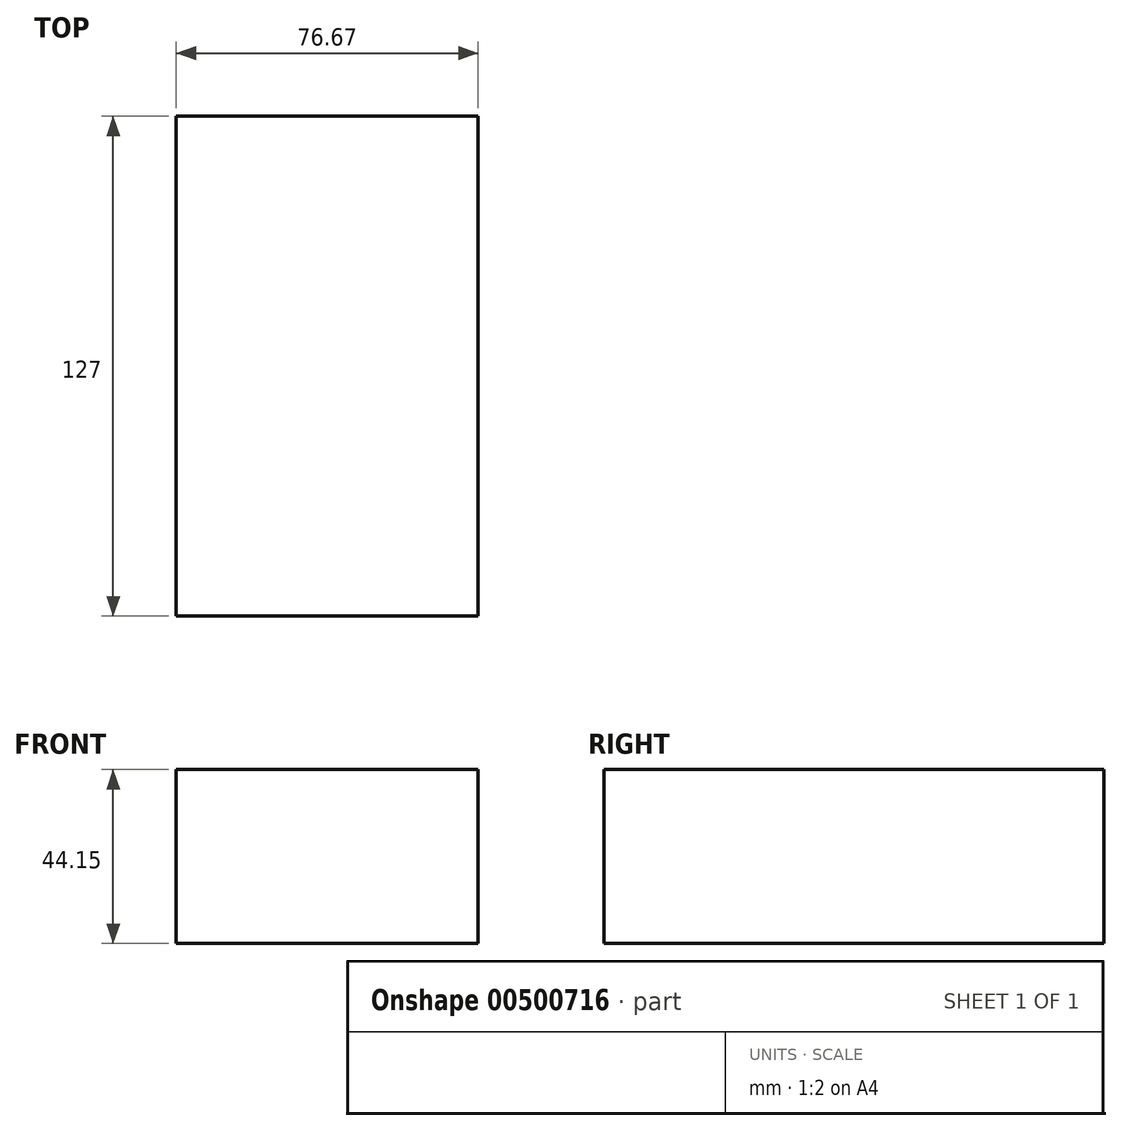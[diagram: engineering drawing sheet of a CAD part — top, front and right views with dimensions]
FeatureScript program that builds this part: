
annotation { "Feature Type Name" : "Feature", "Feature Type Description" : "" }
export const myFeature = defineFeature(function(context is Context, id is Id, definition is map)
    precondition{}
    {
        {
            var Q0;
            Q0=qCreatedBy(makeId("Front.planeOp"),FACE);
            var sketch = newSketch(context, id + "F0", { "sketchPlane" : qUnion([Q0])});
            skLineSegment(sketch, "E0.bottom", {"start": v(-36.6, 22.22) * mm, "end": v(40.08, 22.22) * mm});
            skLineSegment(sketch, "E0.top", {"start": v(-36.6, -21.93) * mm, "end": v(40.08, -21.93) * mm});
            skLineSegment(sketch, "E0.left", {"start": v(-36.6, 22.22) * mm, "end": v(-36.6, -21.93) * mm});
            skLineSegment(sketch, "E0.right", {"start": v(40.08, 22.22) * mm, "end": v(40.08, -21.93) * mm});
            skSolve(sketch);
        }
        {
            var Q0;
            Q0=makeQuery(id+"F0.imprint","IMPRINT",FACE,{"disambiguationData":[TD([[makeQuery(id+"F0.imprint","IMPRINT",EDGE,{"derivedFrom":sQuery(id+"F0.wireOp",EDGE,"E0.bottom")}),-1.0]])]});
            extrude(context, id + "F1", {"entities" : qUnion([Q0]), "depth" : 127 * mm});
        }
    });
